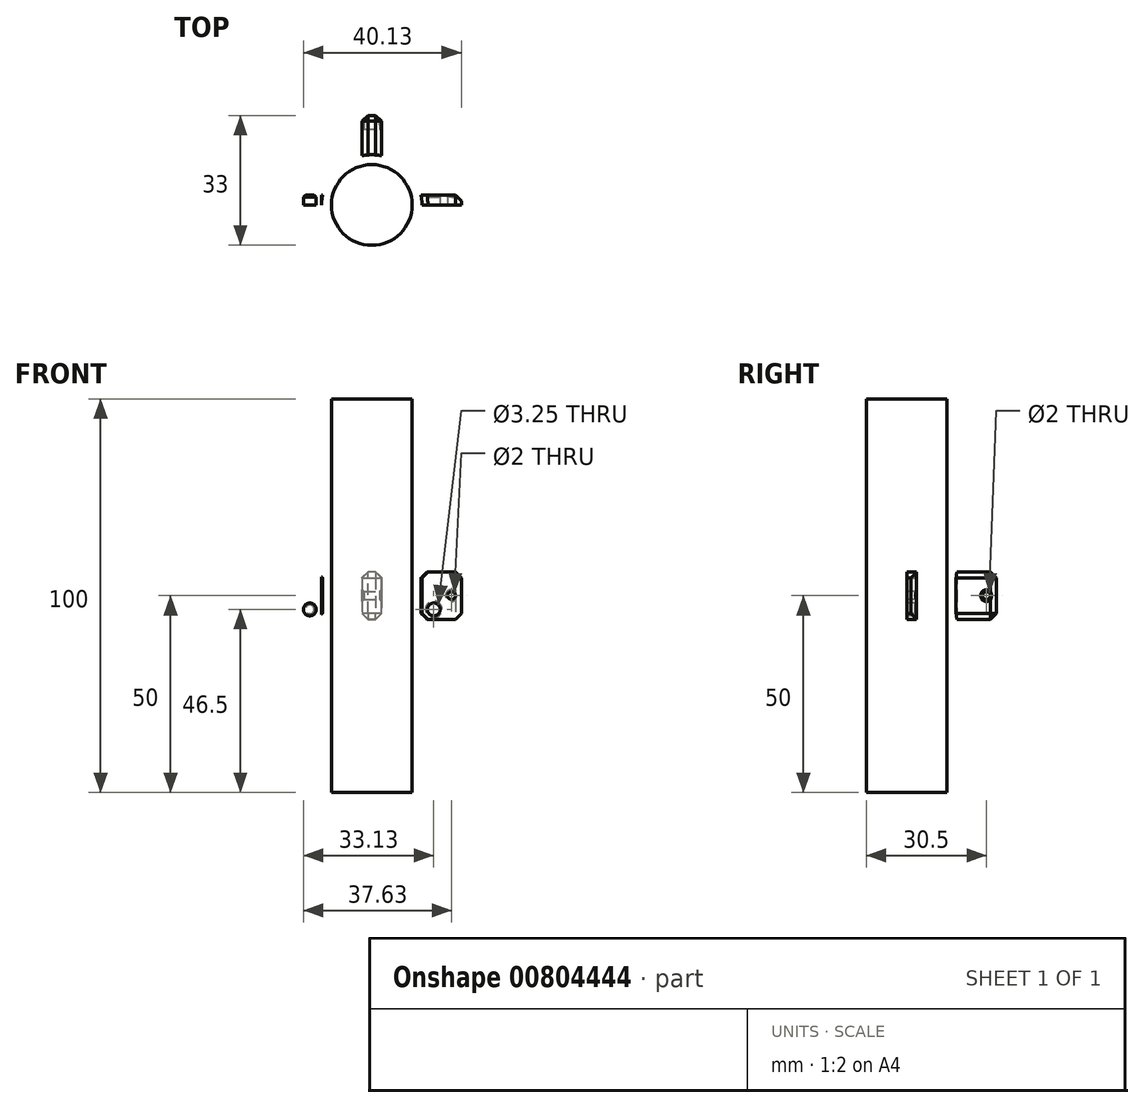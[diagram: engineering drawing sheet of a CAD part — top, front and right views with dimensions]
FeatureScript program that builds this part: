
annotation { "Feature Type Name" : "Feature", "Feature Type Description" : "" }
export const myFeature = defineFeature(function(context is Context, id is Id, definition is map)
    precondition{}
    {
        {
            var Q0;
            Q0=qCreatedBy(makeId("Top.planeOp"),FACE);
            var sketch = newSketch(context, id + "F0", { "sketchPlane" : qUnion([Q0])});
            skCircle(sketch, "E0", {"center": v(0, 0) * mm, "radius": 10.25 * mm});
            skSolve(sketch);
        }
        {
            var Q0;
            Q0=makeQuery(id+"F0.imprint","IMPRINT",FACE,{"disambiguationData":[TD([[makeQuery(id+"F0.imprint","IMPRINT",EDGE,{"derivedFrom":sQuery(id+"F0.wireOp",EDGE,"E0")}),1.0]])]});
            extrude(context, id + "F1", {"entities" : qUnion([Q0]), "endBound" : BoundingType.SYMMETRIC, "depth" : 100 * mm, "offsetDistance" : 25 * mm});
        }
        {
            var Q0;
            Q0=qCreatedBy(makeId("Top.planeOp"),FACE);
            var sketch = newSketch(context, id + "F2", { "sketchPlane" : qUnion([Q0])});
            skArc(sketch, "E1", {"start": v(-10.25, 0) * mm, "mid": v(0, 10.25) * mm, "end": v(10.25, 0) * mm});
            skArc(sketch, "E2", {"start": v(-12.75, 0) * mm, "mid": v(0, 12.75) * mm, "end": v(12.75, 0) * mm});
            skLineSegment(sketch, "E3", {"start": v(-10.25, 0) * mm, "end": v(-12.75, 0) * mm});
            skLineSegment(sketch, "E4", {"start": v(-12.75, 0) * mm, "end": v(-22.75, 0) * mm});
            skLineSegment(sketch, "E5", {"start": v(-22.75, 0) * mm, "end": v(-22.75, 2.5) * mm});
            skLineSegment(sketch, "E6", {"start": v(-22.75, 2.5) * mm, "end": v(-12.5, 2.5) * mm});
            skLineSegment(sketch, "E7.MirrorCS", {"start": v(10.25, 0) * mm, "end": v(12.75, 0) * mm});
            skLineSegment(sketch, "E8.MirrorCS", {"start": v(22.75, 2.5) * mm, "end": v(12.5, 2.5) * mm});
            skLineSegment(sketch, "E9.MirrorCS", {"start": v(22.75, 0) * mm, "end": v(22.75, 2.5) * mm});
            skLineSegment(sketch, "E10.MirrorCS", {"start": v(12.75, 0) * mm, "end": v(22.75, 0) * mm});
            skLineSegment(sketch, "E11", {"start": v(-9.02, 9.02) * mm, "end": v(-16.09, 16.09) * mm});
            skLineSegment(sketch, "E12", {"start": v(-10.5, 7.23) * mm, "end": v(-17.82, 14.29) * mm});
            skLineSegment(sketch, "E13", {"start": v(-17.82, 14.29) * mm, "end": v(-14.35, 17.89) * mm});
            skLineSegment(sketch, "E14", {"start": v(-14.35, 17.89) * mm, "end": v(-6.9, 10.72) * mm});
            skPoint(sketch, "E15", {"position": v(-16.09, 16.09) * mm});
            skLineSegment(sketch, "E16.MirrorCS", {"start": v(14.35, 17.89) * mm, "end": v(6.9, 10.72) * mm});
            skLineSegment(sketch, "E17.MirrorCS", {"start": v(9.02, 9.02) * mm, "end": v(16.09, 16.09) * mm});
            skLineSegment(sketch, "E18.MirrorCS", {"start": v(10.5, 7.23) * mm, "end": v(17.82, 14.29) * mm});
            skLineSegment(sketch, "E19.MirrorCS", {"start": v(17.82, 14.29) * mm, "end": v(14.35, 17.89) * mm});
            skLineSegment(sketch, "E20", {"start": v(0, 12.75) * mm, "end": v(0, 22.75) * mm});
            skLineSegment(sketch, "E21", {"start": v(-2.5, 12.5) * mm, "end": v(-2.5, 22.75) * mm});
            skLineSegment(sketch, "E22", {"start": v(-2.5, 22.75) * mm, "end": v(2.5, 22.75) * mm});
            skLineSegment(sketch, "E23", {"start": v(2.5, 22.75) * mm, "end": v(2.5, 12.5) * mm});
            skPoint(sketch, "E24", {"position": v(0, 22.75) * mm});
            skSolve(sketch);
        }
        {
            var Q0;
            {var subQ0=sQuery(id+"F2.wireOp",EDGE,"E20");Q0=makeQuery(id+"F2.imprint","IMPRINT",FACE,{"disambiguationData":[TD([[makeQuery(id+"F2.imprint","IMPRINT",EDGE,{"derivedFrom":subQ0}),1.0]])]});}
            var Q1;
            {var subQ0=sQuery(id+"F2.wireOp",EDGE,"E20");Q1=makeQuery(id+"F2.imprint","IMPRINT",FACE,{"disambiguationData":[TD([[makeQuery(id+"F2.imprint","IMPRINT",EDGE,{"derivedFrom":subQ0}),-1.0]])]});}
            var Q2;
            Q2=makeQuery(id+"F2.imprint","IMPRINT",FACE,{"disambiguationData":[TD([[makeQuery(id+"F2.imprint","IMPRINT",EDGE,{"derivedFrom":sQuery(id+"F2.wireOp",EDGE,"E1")}),1.0]])]});
            var Q3;
            {var subQ2=sQuery(id+"F2.wireOp",EDGE,"E8.MirrorCS");Q3=makeQuery(id+"F2.imprint","IMPRINT",FACE,{"disambiguationData":[TD([[makeQuery(id+"F2.imprint","IMPRINT",EDGE,{"derivedFrom":subQ2}),1.0]])]});}
            var Q4;
            {var subQ0=sQuery(id+"F2.wireOp",EDGE,"E4");Q4=makeQuery(id+"F2.imprint","IMPRINT",FACE,{"disambiguationData":[TD([[makeQuery(id+"F2.imprint","IMPRINT",EDGE,{"derivedFrom":subQ0}),-1.0]])]});}
            extrude(context, id + "F3", {"entities" : qUnion([Q0, Q1, Q2, Q3, Q4]), "endBound" : BoundingType.SYMMETRIC, "depth" : 12 * mm, "offsetDistance" : 25 * mm});
        }
        {
            var Q0;
            Q0=makeQuery(id+"F3.opExtrude","SWEPT_FACE",FACE,{"disambiguationData":[OSD([sQuery(id+"F2.wireOp",EDGE,"E3"),sQuery(id+"F2.wireOp",EDGE,"E4")])]});
            var sketch = newSketch(context, id + "F4", { "sketchPlane" : qUnion([Q0])});
            skCircle(sketch, "E25", {"center": v(-15.75, 3.5) * mm, "radius": 1.63 * mm});
            skCircle(sketch, "E26.MirrorC", {"center": v(-15.75, -3.5) * mm, "radius": 1.63 * mm});
            skCircle(sketch, "E27.MirrorC", {"center": v(15.75, 3.5) * mm, "radius": 1.63 * mm});
            skCircle(sketch, "E28.MirrorC", {"center": v(15.75, -3.5) * mm, "radius": 1.63 * mm});
            skCircle(sketch, "E29", {"center": v(-20.25, 0) * mm, "radius": 1 * mm});
            skCircle(sketch, "E30.MirrorC", {"center": v(20.25, 0) * mm, "radius": 1 * mm});
            skSolve(sketch);
        }
        {
            var Q0;
            Q0=makeQuery(id+"F4.imprint","IMPRINT",FACE,{"disambiguationData":[TD([[makeQuery(id+"F4.imprint","IMPRINT",EDGE,{"derivedFrom":sQuery(id+"F4.wireOp",EDGE,"E25")}),1.0]])]});
            var Q1;
            Q1=makeQuery(id+"F4.imprint","IMPRINT",FACE,{"disambiguationData":[TD([[makeQuery(id+"F4.imprint","IMPRINT",EDGE,{"derivedFrom":sQuery(id+"F4.wireOp",EDGE,"E26.MirrorC")}),-1.0]])]});
            var Q2;
            Q2=makeQuery(id+"F4.imprint","IMPRINT",FACE,{"disambiguationData":[TD([[makeQuery(id+"F4.imprint","IMPRINT",EDGE,{"derivedFrom":sQuery(id+"F4.wireOp",EDGE,"E27.MirrorC")}),-1.0]])]});
            var Q3;
            Q3=makeQuery(id+"F4.imprint","IMPRINT",FACE,{"disambiguationData":[TD([[makeQuery(id+"F4.imprint","IMPRINT",EDGE,{"derivedFrom":sQuery(id+"F4.wireOp",EDGE,"E28.MirrorC")}),1.0]])]});
            extrude(context, id + "F5", {"entities" : qUnion([Q0, Q1, Q2, Q3]), "operationType" : NewBodyOperationType.REMOVE, "endBound" : BoundingType.SYMMETRIC, "oppositeDirection" : true, "depth" : 25 * mm, "offsetDistance" : 25 * mm});
        }
        {
            var Q0;
            Q0=makeQuery(id+"F4.imprint","IMPRINT",FACE,{"disambiguationData":[TD([[makeQuery(id+"F4.imprint","IMPRINT",EDGE,{"derivedFrom":sQuery(id+"F4.wireOp",EDGE,"E29")}),1.0]])]});
            extrude(context, id + "F6", {"entities" : qUnion([Q0]), "endBound" : BoundingType.SYMMETRIC, "depth" : 25 * mm, "offsetDistance" : 25 * mm});
        }
        {
            var Q0;
            Q0=makeQuery(id+"F6.opExtrude","SWEPT_BODY",BODY,{"disambiguationData":[OSD([sQuery(id+"F4.wireOp",EDGE,"E29")])]});
            var Q1;
            Q1=makeQuery(id+"F1.opExtrude","CAP_EDGE",EDGE,{"disambiguationData":[OSD([sQuery(id+"F0.wireOp",EDGE,"E0")])],"isStart":false});
            circularPattern(context, id + "F7", {"entities" : qUnion([Q0]), "axis" : qUnion([Q1]), "angle" : 360 * degree, "instanceCount" : 4, "equalSpace" : true});
        }
        {
            var Q0;
            Q0=makeQuery(id+"F7.opPattern","COPY",BODY,{"derivedFrom":makeQuery(id+"F6.opExtrude","SWEPT_BODY",BODY,{"disambiguationData":[OSD([sQuery(id+"F4.wireOp",EDGE,"E29")])]}),"instanceName":"1"});
            deleteBodies(context, id + "F8", {"entities" : qUnion([Q0])});
        }
        {
            var Q0;
            Q0=makeQuery(id+"F7.opPattern","COPY",BODY,{"derivedFrom":makeQuery(id+"F6.opExtrude","SWEPT_BODY",BODY,{"disambiguationData":[OSD([sQuery(id+"F4.wireOp",EDGE,"E29")])]}),"instanceName":"3"});
            var Q1;
            Q1=makeQuery(id+"F6.opExtrude","SWEPT_BODY",BODY,{"disambiguationData":[OSD([sQuery(id+"F4.wireOp",EDGE,"E29")])]});
            var Q2;
            Q2=makeQuery(id+"F7.opPattern","COPY",BODY,{"derivedFrom":makeQuery(id+"F6.opExtrude","SWEPT_BODY",BODY,{"disambiguationData":[OSD([sQuery(id+"F4.wireOp",EDGE,"E29")])]}),"instanceName":"2"});
            var Q3;
            Q3=makeQuery(id+"F3.opExtrude","SWEPT_BODY",BODY,{"disambiguationData":[OSD([sQuery(id+"F2.wireOp",EDGE,"E1"),sQuery(id+"F2.wireOp",EDGE,"E2"),sQuery(id+"F2.wireOp",EDGE,"E3"),sQuery(id+"F2.wireOp",EDGE,"E4"),sQuery(id+"F2.wireOp",EDGE,"E5"),sQuery(id+"F2.wireOp",EDGE,"E6"),sQuery(id+"F2.wireOp",EDGE,"E7.MirrorCS"),sQuery(id+"F2.wireOp",EDGE,"E8.MirrorCS"),sQuery(id+"F2.wireOp",EDGE,"E9.MirrorCS"),sQuery(id+"F2.wireOp",EDGE,"E10.MirrorCS"),sQuery(id+"F2.wireOp",EDGE,"E21"),sQuery(id+"F2.wireOp",EDGE,"E22"),sQuery(id+"F2.wireOp",EDGE,"E23")])]});
            booleanBodies(context, id + "F9", {"operationType" : BooleanOperationType.SUBTRACTION, "tools" : qUnion([Q0, Q1, Q2]), "targets" : qUnion([Q3])});
        }
        {
            var Q0;
            Q0=makeQuery(id+"F3.opExtrude","CAP_EDGE",EDGE,{"disambiguationData":[OSD([sQuery(id+"F2.wireOp",EDGE,"E9.MirrorCS")])],"isStart":false});
            var Q1;
            Q1=makeQuery(id+"F3.opExtrude","CAP_EDGE",EDGE,{"disambiguationData":[OSD([sQuery(id+"F2.wireOp",EDGE,"E9.MirrorCS")])],"isStart":true});
            var Q2;
            Q2=makeQuery(id+"F3.opExtrude","CAP_EDGE",EDGE,{"disambiguationData":[OSD([sQuery(id+"F2.wireOp",EDGE,"E22")])],"isStart":true});
            var Q3;
            Q3=makeQuery(id+"F3.opExtrude","CAP_EDGE",EDGE,{"disambiguationData":[OSD([sQuery(id+"F2.wireOp",EDGE,"E22")])],"isStart":false});
            var Q4;
            Q4=makeQuery(id+"F3.opExtrude","CAP_EDGE",EDGE,{"disambiguationData":[OSD([sQuery(id+"F2.wireOp",EDGE,"E23")])],"isStart":false});
            var Q5;
            Q5=makeQuery(id+"F3.opExtrude","CAP_EDGE",EDGE,{"disambiguationData":[OSD([sQuery(id+"F2.wireOp",EDGE,"E21")])],"isStart":false});
            var Q6;
            {var subQ0=sQuery(id+"F2.wireOp",EDGE,"E2");var subQ2=makeQuery(id+"F2.imprint","INTERSECT",VERTEX,{"derivedFrom":[subQ0,sQuery(id+"F2.wireOp",EDGE,"E17.MirrorCS")]});var subQ3=makeQuery(id+"F2.imprint","INTERSECT",VERTEX,{"derivedFrom":[subQ0,sQuery(id+"F2.wireOp",EDGE,"E16.MirrorCS")]});Q6=makeQuery(id+"F3.opExtrude","CAP_EDGE",EDGE,{"disambiguationData":[OSD([subQ0]),TDD([makeQuery(id+"F2.imprint","IMPRINT",EDGE,{"disambiguationData":[TD([[subQ3,1.0]])],"derivedFrom":subQ0}),makeQuery(id+"F2.imprint","IMPRINT",EDGE,{"disambiguationData":[TD([[subQ3,-1.0]])],"derivedFrom":subQ0}),makeQuery(id+"F2.imprint","IMPRINT",EDGE,{"disambiguationData":[TD([[subQ2,-1.0]])],"derivedFrom":subQ0}),makeQuery(id+"F2.imprint","IMPRINT",EDGE,{"disambiguationData":[TD([[makeQuery(id+"F2.imprint","INTERSECT",VERTEX,{"derivedFrom":[subQ0,sQuery(id+"F2.wireOp",EDGE,"E8.MirrorCS")]}),1.0]])],"derivedFrom":subQ0})])],"isStart":false});}
            var Q7;
            {var subQ0=sQuery(id+"F2.wireOp",EDGE,"E2");var subQ1=makeQuery(id+"F2.imprint","INTERSECT",VERTEX,{"derivedFrom":[subQ0,sQuery(id+"F2.wireOp",EDGE,"E14")]});var subQ2=makeQuery(id+"F2.imprint","INTERSECT",VERTEX,{"derivedFrom":[subQ0,sQuery(id+"F2.wireOp",EDGE,"E11")]});Q7=makeQuery(id+"F3.opExtrude","CAP_EDGE",EDGE,{"disambiguationData":[OSD([subQ0]),TDD([makeQuery(id+"F2.imprint","IMPRINT",EDGE,{"disambiguationData":[TD([[makeQuery(id+"F2.imprint","INTERSECT",VERTEX,{"derivedFrom":[subQ0,sQuery(id+"F2.wireOp",EDGE,"E6")]}),-1.0]])],"derivedFrom":subQ0}),makeQuery(id+"F2.imprint","IMPRINT",EDGE,{"disambiguationData":[TD([[subQ2,1.0]])],"derivedFrom":subQ0}),makeQuery(id+"F2.imprint","IMPRINT",EDGE,{"disambiguationData":[TD([[subQ2,-1.0]])],"derivedFrom":subQ0}),makeQuery(id+"F2.imprint","IMPRINT",EDGE,{"disambiguationData":[TD([[subQ1,-1.0]])],"derivedFrom":subQ0})])],"isStart":false});}
            var Q8;
            {var subQ0=sQuery(id+"F2.wireOp",EDGE,"E2");var subQ1=makeQuery(id+"F2.imprint","INTERSECT",VERTEX,{"derivedFrom":[subQ0,sQuery(id+"F2.wireOp",EDGE,"E14")]});var subQ2=makeQuery(id+"F2.imprint","INTERSECT",VERTEX,{"derivedFrom":[subQ0,sQuery(id+"F2.wireOp",EDGE,"E11")]});Q8=makeQuery(id+"F3.opExtrude","CAP_EDGE",EDGE,{"disambiguationData":[OSD([subQ0]),TDD([makeQuery(id+"F2.imprint","IMPRINT",EDGE,{"disambiguationData":[TD([[makeQuery(id+"F2.imprint","INTERSECT",VERTEX,{"derivedFrom":[subQ0,sQuery(id+"F2.wireOp",EDGE,"E6")]}),-1.0]])],"derivedFrom":subQ0}),makeQuery(id+"F2.imprint","IMPRINT",EDGE,{"disambiguationData":[TD([[subQ2,1.0]])],"derivedFrom":subQ0}),makeQuery(id+"F2.imprint","IMPRINT",EDGE,{"disambiguationData":[TD([[subQ2,-1.0]])],"derivedFrom":subQ0}),makeQuery(id+"F2.imprint","IMPRINT",EDGE,{"disambiguationData":[TD([[subQ1,-1.0]])],"derivedFrom":subQ0})])],"isStart":true});}
            var Q9;
            Q9=makeQuery(id+"F3.opExtrude","CAP_EDGE",EDGE,{"disambiguationData":[OSD([sQuery(id+"F2.wireOp",EDGE,"E21")])],"isStart":true});
            var Q10;
            Q10=makeQuery(id+"F3.opExtrude","CAP_EDGE",EDGE,{"disambiguationData":[OSD([sQuery(id+"F2.wireOp",EDGE,"E23")])],"isStart":true});
            var Q11;
            {var subQ0=sQuery(id+"F2.wireOp",EDGE,"E2");var subQ2=makeQuery(id+"F2.imprint","INTERSECT",VERTEX,{"derivedFrom":[subQ0,sQuery(id+"F2.wireOp",EDGE,"E17.MirrorCS")]});var subQ3=makeQuery(id+"F2.imprint","INTERSECT",VERTEX,{"derivedFrom":[subQ0,sQuery(id+"F2.wireOp",EDGE,"E16.MirrorCS")]});Q11=makeQuery(id+"F3.opExtrude","CAP_EDGE",EDGE,{"disambiguationData":[OSD([subQ0]),TDD([makeQuery(id+"F2.imprint","IMPRINT",EDGE,{"disambiguationData":[TD([[subQ3,1.0]])],"derivedFrom":subQ0}),makeQuery(id+"F2.imprint","IMPRINT",EDGE,{"disambiguationData":[TD([[subQ3,-1.0]])],"derivedFrom":subQ0}),makeQuery(id+"F2.imprint","IMPRINT",EDGE,{"disambiguationData":[TD([[subQ2,-1.0]])],"derivedFrom":subQ0}),makeQuery(id+"F2.imprint","IMPRINT",EDGE,{"disambiguationData":[TD([[makeQuery(id+"F2.imprint","INTERSECT",VERTEX,{"derivedFrom":[subQ0,sQuery(id+"F2.wireOp",EDGE,"E8.MirrorCS")]}),1.0]])],"derivedFrom":subQ0})])],"isStart":true});}
            var Q12;
            Q12=makeQuery(id+"F3.opExtrude","SWEPT_EDGE",EDGE,{"disambiguationData":[OSD([sQuery(id+"F2.wireOp",EDGE,"E21"),sQuery(id+"F2.wireOp",EDGE,"E22")])]});
            var Q13;
            Q13=makeQuery(id+"F3.opExtrude","SWEPT_EDGE",EDGE,{"disambiguationData":[OSD([sQuery(id+"F2.wireOp",EDGE,"E22"),sQuery(id+"F2.wireOp",EDGE,"E23")])]});
            var Q14;
            Q14=makeQuery(id+"F3.opExtrude","SWEPT_EDGE",EDGE,{"disambiguationData":[OSD([sQuery(id+"F2.wireOp",EDGE,"E5"),sQuery(id+"F2.wireOp",EDGE,"E6")])]});
            var Q15;
            Q15=makeQuery(id+"F3.opExtrude","SWEPT_EDGE",EDGE,{"disambiguationData":[OSD([sQuery(id+"F2.wireOp",EDGE,"E8.MirrorCS"),sQuery(id+"F2.wireOp",EDGE,"E9.MirrorCS")])]});
            chamfer(context, id + "F10", {"entities" : qUnion([Q0, Q1, Q2, Q3, Q4, Q5, Q6, Q7, Q8, Q9, Q10, Q11, Q12, Q13, Q14, Q15]), "width" : 1.5 * mm, "tangentPropagation" : true});
        }
        {
            var Q0;
            Q0=makeQuery(id+"F9.opBoolean","INTERSECT",EDGE,{"derivedFrom":[makeQuery(id+"F3.opExtrude","SWEPT_FACE",FACE,{"disambiguationData":[OSD([sQuery(id+"F2.wireOp",EDGE,"E8.MirrorCS")])]}),makeQuery(id+"F7.opPattern","COPY",FACE,{"derivedFrom":makeQuery(id+"F6.opExtrude","SWEPT_FACE",FACE,{"disambiguationData":[OSD([sQuery(id+"F4.wireOp",EDGE,"E29")])]}),"instanceName":"2"})]});
            var Q1;
            Q1=makeQuery(id+"F9.opBoolean","INTERSECT",EDGE,{"derivedFrom":[makeQuery(id+"F3.opExtrude","SWEPT_FACE",FACE,{"disambiguationData":[OSD([sQuery(id+"F2.wireOp",EDGE,"E23")])]}),makeQuery(id+"F7.opPattern","COPY",FACE,{"derivedFrom":makeQuery(id+"F6.opExtrude","SWEPT_FACE",FACE,{"disambiguationData":[OSD([sQuery(id+"F4.wireOp",EDGE,"E29")])]}),"instanceName":"3"})]});
            var Q2;
            Q2=makeQuery(id+"F9.opBoolean","INTERSECT",EDGE,{"derivedFrom":[makeQuery(id+"F3.opExtrude","SWEPT_FACE",FACE,{"disambiguationData":[OSD([sQuery(id+"F2.wireOp",EDGE,"E21")])]}),makeQuery(id+"F7.opPattern","COPY",FACE,{"derivedFrom":makeQuery(id+"F6.opExtrude","SWEPT_FACE",FACE,{"disambiguationData":[OSD([sQuery(id+"F4.wireOp",EDGE,"E29")])]}),"instanceName":"3"})]});
            var Q3;
            Q3=makeQuery(id+"F5.boolean.opBoolean","INTERSECT",EDGE,{"derivedFrom":[makeQuery(id+"F3.opExtrude","SWEPT_FACE",FACE,{"disambiguationData":[OSD([sQuery(id+"F2.wireOp",EDGE,"E8.MirrorCS")])]}),makeQuery(id+"F5.opExtrude","SWEPT_FACE",FACE,{"disambiguationData":[OSD([sQuery(id+"F4.wireOp",EDGE,"E27.MirrorC")])]})]});
            var Q4;
            Q4=makeQuery(id+"F5.boolean.opBoolean","INTERSECT",EDGE,{"derivedFrom":[makeQuery(id+"F3.opExtrude","SWEPT_FACE",FACE,{"disambiguationData":[OSD([sQuery(id+"F2.wireOp",EDGE,"E8.MirrorCS")])]}),makeQuery(id+"F5.opExtrude","SWEPT_FACE",FACE,{"disambiguationData":[OSD([sQuery(id+"F4.wireOp",EDGE,"E28.MirrorC")])]})]});
            var Q5;
            Q5=makeQuery(id+"F5.boolean.opBoolean","INTERSECT",EDGE,{"derivedFrom":[makeQuery(id+"F3.opExtrude","SWEPT_FACE",FACE,{"disambiguationData":[OSD([sQuery(id+"F2.wireOp",EDGE,"E6")])]}),makeQuery(id+"F5.opExtrude","SWEPT_FACE",FACE,{"disambiguationData":[OSD([sQuery(id+"F4.wireOp",EDGE,"E26.MirrorC")])]})]});
            var Q6;
            Q6=makeQuery(id+"F5.boolean.opBoolean","INTERSECT",EDGE,{"derivedFrom":[makeQuery(id+"F3.opExtrude","SWEPT_FACE",FACE,{"disambiguationData":[OSD([sQuery(id+"F2.wireOp",EDGE,"E6")])]}),makeQuery(id+"F5.opExtrude","SWEPT_FACE",FACE,{"disambiguationData":[OSD([sQuery(id+"F4.wireOp",EDGE,"E25")])]})]});
            var Q7;
            Q7=makeQuery(id+"F9.opBoolean","INTERSECT",EDGE,{"derivedFrom":[makeQuery(id+"F3.opExtrude","SWEPT_FACE",FACE,{"disambiguationData":[OSD([sQuery(id+"F2.wireOp",EDGE,"E6")])]}),makeQuery(id+"F6.opExtrude","SWEPT_FACE",FACE,{"disambiguationData":[OSD([sQuery(id+"F4.wireOp",EDGE,"E29")])]})]});
            chamfer(context, id + "F11", {"entities" : qUnion([Q0, Q1, Q2, Q3, Q4, Q5, Q6, Q7]), "width" : 0.5 * mm, "tangentPropagation" : true});
        }
    });
